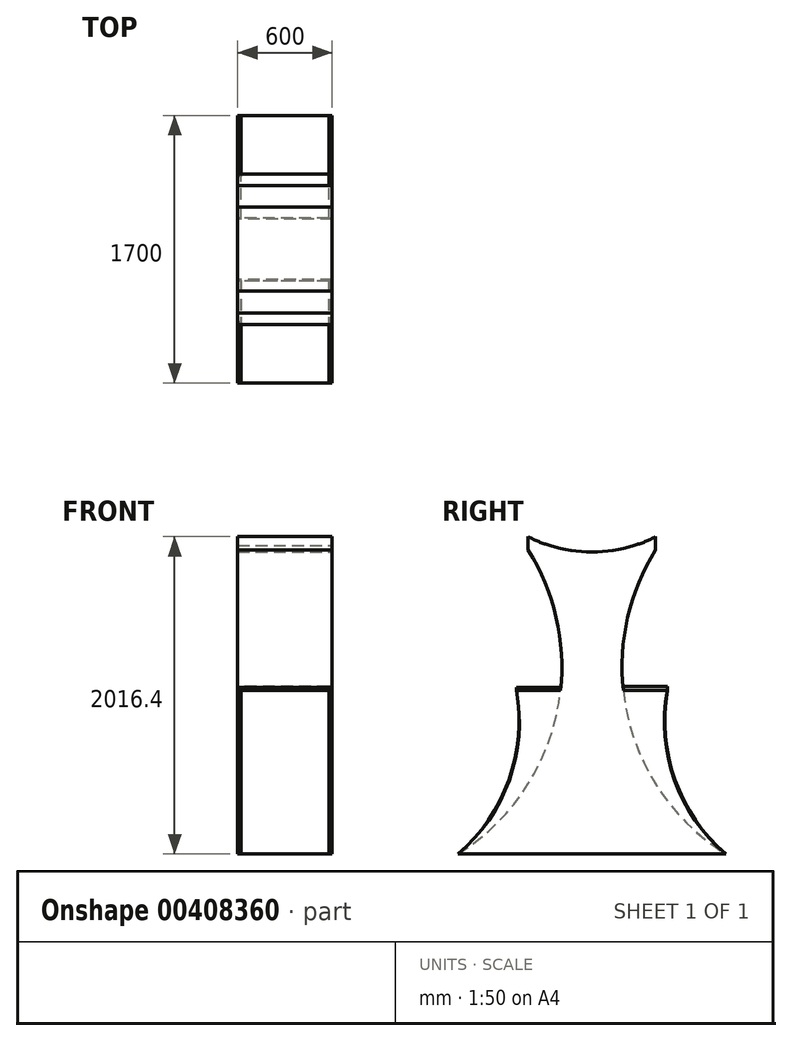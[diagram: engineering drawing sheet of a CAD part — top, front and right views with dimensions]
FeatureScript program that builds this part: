
annotation { "Feature Type Name" : "Feature", "Feature Type Description" : "" }
export const myFeature = defineFeature(function(context is Context, id is Id, definition is map)
    precondition{}
    {
        {
            var Q0;
            Q0=qCreatedBy(makeId("Right.planeOp"),FACE);
            var sketch = newSketch(context, id + "F0", { "sketchPlane" : qUnion([Q0])});
            skLineSegment(sketch, "E0", {"start": v(-858.66, 1.3) * mm, "end": v(841.34, 1.3) * mm});
            skPoint(sketch, "E1.end.orphan", {"position": v(0, 1171.1) * mm});
            skArc(sketch, "E2", {"start": v(-413.77, 2017.7) * mm, "mid": v(-217.07, 1948.77) * mm, "end": v(-8.66, 1951.3) * mm});
            skArc(sketch, "E3", {"start": v(-8.66, 1951.3) * mm, "mid": v(199.75, 1948.77) * mm, "end": v(396.44, 2017.7) * mm});
            skLineSegment(sketch, "E4", {"start": v(-413.77, 2017.7) * mm, "end": v(-413.77, 1932.7) * mm});
            skLineSegment(sketch, "E5", {"start": v(396.44, 2017.7) * mm, "end": v(396.44, 1932.7) * mm});
            skArc(sketch, "E6", {"start": v(-858.66, 1.3) * mm, "mid": v(-235.62, 874.72) * mm, "end": v(-413.77, 1932.7) * mm});
            skArc(sketch, "E7", {"start": v(396.44, 1932.7) * mm, "mid": v(218.29, 874.72) * mm, "end": v(841.34, 1.3) * mm});
            skPoint(sketch, "E8.start.orphan", {"position": v(-8.66, 1.3) * mm});
            skSolve(sketch);
        }
        {
            var Q0;
            Q0=makeQuery(id+"F0.imprint","IMPRINT",FACE,{"disambiguationData":[TD([[makeQuery(id+"F0.imprint","IMPRINT",EDGE,{"derivedFrom":sQuery(id+"F0.wireOp",EDGE,"E0")}),1.0]])]});
            extrude(context, id + "F1", {"entities" : qUnion([Q0]), "depth" : 600 * mm});
        }
        {
            var Q0;
            Q0=makeQuery(id+"F1.opExtrude","CAP_FACE",FACE,{"disambiguationData":[OSD([sQuery(id+"F0.wireOp",EDGE,"E0"),sQuery(id+"F0.wireOp",EDGE,"E2"),sQuery(id+"F0.wireOp",EDGE,"E3"),sQuery(id+"F0.wireOp",EDGE,"E4"),sQuery(id+"F0.wireOp",EDGE,"E5"),sQuery(id+"F0.wireOp",EDGE,"E6"),sQuery(id+"F0.wireOp",EDGE,"E7")])],"isStart":false});
            var sketch = newSketch(context, id + "F2", { "sketchPlane" : qUnion([Q0])});
            skArc(sketch, "E9", {"start": v(-413.77, 2017.7) * mm, "mid": v(-8.66, 1920.6) * mm, "end": v(396.44, 2017.7) * mm});
            skLineSegment(sketch, "E10", {"start": v(-413.77, 2017.7) * mm, "end": v(396.44, 2017.7) * mm});
            skSolve(sketch);
        }
        {
            var Q0;
            {var subQ0=sQuery(id+"F2.wireOp",EDGE,"E10");Q0=makeQuery(id+"F2.imprint","IMPRINT",FACE,{"disambiguationData":[TD([[makeQuery(id+"F2.imprint","IMPRINT",EDGE,{"derivedFrom":subQ0}),-1.0]])]});}
            var Q1;
            {var subQ0=sQuery(id+"F2.wireOp",EDGE,"E9");var subQ1=makeQuery(id+"F1.opExtrude","CAP_EDGE",EDGE,{"disambiguationData":[OSD([sQuery(id+"F0.wireOp",EDGE,"E2")])],"isStart":false});var subQ2=makeQuery(id+"F2.imprint","INTERSECT",VERTEX,{"derivedFrom":[subQ1,subQ0]});Q1=makeQuery(id+"F2.imprint","IMPRINT",FACE,{"disambiguationData":[TD([[makeQuery(id+"F2.imprint","IMPRINT",EDGE,{"disambiguationData":[TD([[subQ2,-1.0]])],"derivedFrom":subQ0}),1.0]])]});}
            extrude(context, id + "F3", {"entities" : qUnion([Q0, Q1]), "operationType" : NewBodyOperationType.REMOVE, "endBound" : BoundingType.THROUGH_ALL, "oppositeDirection" : true, "depth" : 25 * mm});
        }
        {
            var Q0;
            Q0=makeQuery(id+"F1.opExtrude","CAP_FACE",FACE,{"disambiguationData":[OSD([sQuery(id+"F0.wireOp",EDGE,"E0"),sQuery(id+"F0.wireOp",EDGE,"E2"),sQuery(id+"F0.wireOp",EDGE,"E3"),sQuery(id+"F0.wireOp",EDGE,"E4"),sQuery(id+"F0.wireOp",EDGE,"E5"),sQuery(id+"F0.wireOp",EDGE,"E6"),sQuery(id+"F0.wireOp",EDGE,"E7")])],"isStart":false});
            var sketch = newSketch(context, id + "F4", { "sketchPlane" : qUnion([Q0])});
            skArc(sketch, "E11", {"start": v(-858.66, 1.3) * mm, "mid": v(-533.5, 470.59) * mm, "end": v(-487.87, 1039.7) * mm});
            skLineSegment(sketch, "E12", {"start": v(-487.87, 1039.7) * mm, "end": v(-207.87, 1039.7) * mm});
            skLineSegment(sketch, "E13", {"start": v(190.54, 1039.7) * mm, "end": v(470.54, 1039.7) * mm});
            skArc(sketch, "E14", {"start": v(470.54, 1039.7) * mm, "mid": v(516.17, 470.59) * mm, "end": v(841.34, 1.3) * mm});
            skSolve(sketch);
        }
        {
            var Q0;
            {var subQ0=sQuery(id+"F4.wireOp",EDGE,"E11");Q0=makeQuery(id+"F4.imprint","IMPRINT",FACE,{"disambiguationData":[TD([[makeQuery(id+"F4.imprint","IMPRINT",EDGE,{"derivedFrom":subQ0}),-1.0]])]});}
            var Q1;
            {var subQ0=sQuery(id+"F4.wireOp",EDGE,"E13");Q1=makeQuery(id+"F4.imprint","IMPRINT",FACE,{"disambiguationData":[TD([[makeQuery(id+"F4.imprint","IMPRINT",EDGE,{"derivedFrom":subQ0}),-1.0]])]});}
            extrude(context, id + "F5", {"entities" : qUnion([Q0, Q1]), "operationType" : NewBodyOperationType.ADD, "oppositeDirection" : true, "depth" : 20 * mm});
        }
        {
            var Q0;
            Q0=makeQuery(id+"F1.opExtrude","CAP_FACE",FACE,{"disambiguationData":[OSD([sQuery(id+"F0.wireOp",EDGE,"E0"),sQuery(id+"F0.wireOp",EDGE,"E2"),sQuery(id+"F0.wireOp",EDGE,"E3"),sQuery(id+"F0.wireOp",EDGE,"E4"),sQuery(id+"F0.wireOp",EDGE,"E5"),sQuery(id+"F0.wireOp",EDGE,"E6"),sQuery(id+"F0.wireOp",EDGE,"E7")])],"isStart":true});
            var sketch = newSketch(context, id + "F6", { "sketchPlane" : qUnion([Q0])});
            skLineSegment(sketch, "E15", {"start": v(-190.65, 1038.7) * mm, "end": v(-470.65, 1038.7) * mm});
            skLineSegment(sketch, "E16", {"start": v(207.88, 1039.64) * mm, "end": v(487.88, 1039.64) * mm});
            skArc(sketch, "E17", {"start": v(-841.34, 1.3) * mm, "mid": v(-519.68, 471.3) * mm, "end": v(-470.65, 1038.7) * mm});
            skArc(sketch, "E18", {"start": v(487.88, 1039.64) * mm, "mid": v(536.71, 471.7) * mm, "end": v(858.66, 1.3) * mm});
            skSolve(sketch);
        }
        {
            var Q0;
            {var subQ0=sQuery(id+"F6.wireOp",EDGE,"E15");Q0=makeQuery(id+"F6.imprint","IMPRINT",FACE,{"disambiguationData":[TD([[makeQuery(id+"F6.imprint","IMPRINT",EDGE,{"derivedFrom":subQ0}),1.0]])]});}
            var Q1;
            {var subQ0=sQuery(id+"F6.wireOp",EDGE,"E16");Q1=makeQuery(id+"F6.imprint","IMPRINT",FACE,{"disambiguationData":[TD([[makeQuery(id+"F6.imprint","IMPRINT",EDGE,{"derivedFrom":subQ0}),-1.0]])]});}
            extrude(context, id + "F7", {"entities" : qUnion([Q0, Q1]), "operationType" : NewBodyOperationType.ADD, "oppositeDirection" : true, "depth" : 20 * mm});
        }
        {
            var Q0;
            Q0=makeQuery(id+"F5.opExtrude","SWEPT_FACE",FACE,{"disambiguationData":[OSD([sQuery(id+"F4.wireOp",EDGE,"E13")])]});
            var sketch = newSketch(context, id + "F8", { "sketchPlane" : qUnion([Q0])});
            skLineSegment(sketch, "E19", {"start": v(600, 190.54) * mm, "end": v(0, 190.54) * mm});
            skLineSegment(sketch, "E20", {"start": v(0, 190.54) * mm, "end": v(0, 470.54) * mm});
            skLineSegment(sketch, "E21", {"start": v(0, 470.54) * mm, "end": v(600, 470.54) * mm});
            skLineSegment(sketch, "E22", {"start": v(600, 470.54) * mm, "end": v(600, 190.54) * mm});
            skSolve(sketch);
        }
        {
            var Q0;
            {var subQ2=sQuery(id+"F8.wireOp",EDGE,"E20");Q0=makeQuery(id+"F8.imprint","IMPRINT",FACE,{"disambiguationData":[TD([[makeQuery(id+"F8.imprint","IMPRINT",EDGE,{"derivedFrom":subQ2}),-1.0]])]});}
            extrude(context, id + "F9", {"entities" : qUnion([Q0]), "depth" : 25 * mm});
        }
        {
            var Q0;
            Q0=makeQuery(id+"F9.opExtrude","SWEPT_FACE",FACE,{"disambiguationData":[OSD([sQuery(id+"F4.wireOp",EDGE,"E13")])]});
            extrude(context, id + "F10", {"entities" : qUnion([Q0]), "depth" : 20 * mm});
        }
        {
            var Q0;
            Q0=makeQuery(id+"F7.opExtrude","SWEPT_FACE",FACE,{"disambiguationData":[OSD([sQuery(id+"F6.wireOp",EDGE,"E16")])]});
            var sketch = newSketch(context, id + "F11", { "sketchPlane" : qUnion([Q0])});
            skLineSegment(sketch, "E23", {"start": v(0, -487.88) * mm, "end": v(598.82, -487.88) * mm});
            skLineSegment(sketch, "E24", {"start": v(598.82, -487.88) * mm, "end": v(598.82, -209.16) * mm});
            skLineSegment(sketch, "E25", {"start": v(598.82, -209.16) * mm, "end": v(0, -209.16) * mm});
            skLineSegment(sketch, "E26", {"start": v(0, -209.16) * mm, "end": v(0, -487.88) * mm});
            skSolve(sketch);
        }
        {
            var Q0;
            {var subQ0=sQuery(id+"F11.wireOp",EDGE,"E26");Q0=makeQuery(id+"F11.imprint","IMPRINT",FACE,{"disambiguationData":[TD([[makeQuery(id+"F11.imprint","IMPRINT",EDGE,{"derivedFrom":subQ0}),1.0]])]});}
            var Q1;
            {var subQ3=sQuery(id+"F11.wireOp",EDGE,"E24");Q1=makeQuery(id+"F11.imprint","IMPRINT",FACE,{"disambiguationData":[TD([[makeQuery(id+"F11.imprint","IMPRINT",EDGE,{"derivedFrom":subQ3}),1.0]])]});}
            extrude(context, id + "F12", {"entities" : qUnion([Q0, Q1]), "operationType" : NewBodyOperationType.ADD, "depth" : 20 * mm});
        }
    });
